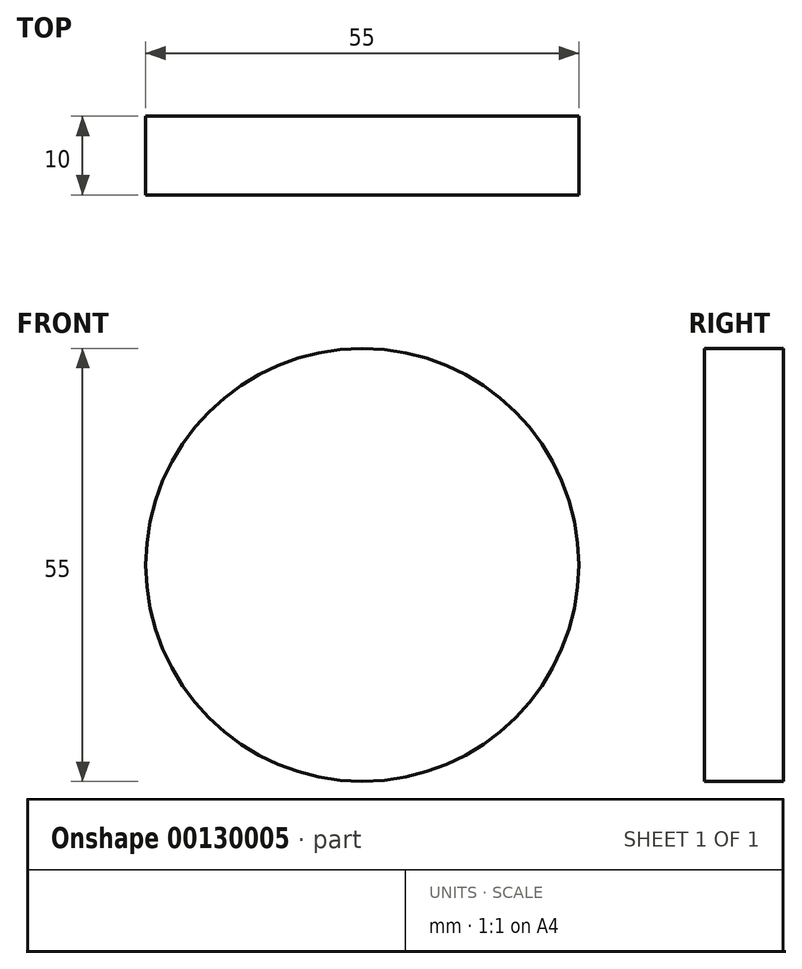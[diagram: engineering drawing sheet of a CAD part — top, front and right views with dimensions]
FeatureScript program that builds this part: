
annotation { "Feature Type Name" : "Feature", "Feature Type Description" : "" }
export const myFeature = defineFeature(function(context is Context, id is Id, definition is map)
    precondition{}
    {
        {
            var Q0;
            Q0=qCreatedBy(makeId("Front.planeOp"),FACE);
            var sketch = newSketch(context, id + "F0", { "sketchPlane" : qUnion([Q0])});
            skCircle(sketch, "E0", {"center": v(-22.92, 28.27) * mm, "radius": 27.5 * mm});
            skSolve(sketch);
        }
        {
            var Q0;
            Q0 = qSketchRegion(id + "F0", true);
            extrude(context, id + "F1", {"entities" : qUnion([Q0]), "depth" : 10 * mm});
        }
    });
